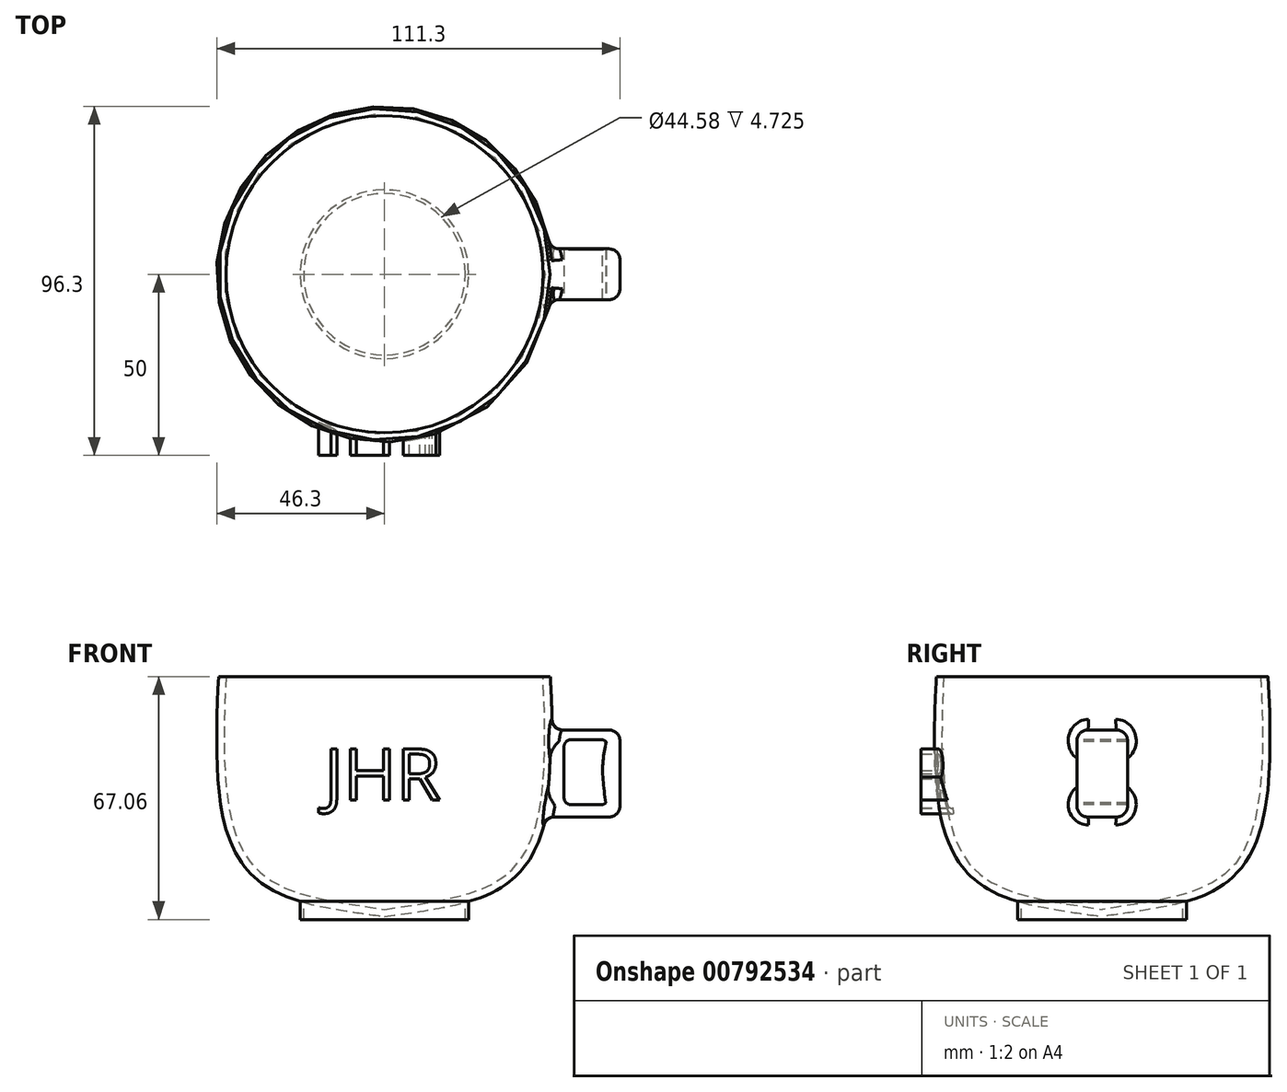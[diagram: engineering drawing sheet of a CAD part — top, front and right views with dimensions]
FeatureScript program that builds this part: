
annotation { "Feature Type Name" : "Feature", "Feature Type Description" : "" }
export const myFeature = defineFeature(function(context is Context, id is Id, definition is map)
    precondition{}
    {
        {
            var Q0;
            Q0=qCreatedBy(makeId("Front.planeOp"),FACE);
            var sketch = newSketch(context, id + "F0", { "sketchPlane" : qUnion([Q0])});
            skFitSpline(sketch, "E0", {"points": [v(-4.5, -38.34) * mm, v(36.26, -25.42) * mm, v(43.52, 31.56) * mm], "startDerivative": vector(104.57, 20.01) * mm, "endDerivative": vector(-6, 125.75) * mm});
            skFitSpline(sketch, "E1.0", {"points": [v(-4.13, -40.3) * mm, v(0.17, -39.48) * mm, v(6.7, -38.54) * mm, v(15.07, -37.17) * mm, v(21.07, -35.9) * mm, v(26.7, -34.18) * mm, v(30.98, -32.2) * mm, v(34.08, -30.19) * mm, v(35.86, -28.72) * mm, v(37.18, -27.4) * mm, v(38.42, -26) * mm, v(39.8, -24.1) * mm, v(41.23, -21.58) * mm, v(42.84, -17.96) * mm, v(44.34, -12.98) * mm, v(45.48, -6.4) * mm, v(46.1, 0.69) * mm, v(46.3, 8.15) * mm, v(46.16, 18.46) * mm, v(45.77, 26.42) * mm, v(45.52, 31.66) * mm]});
            skLineSegment(sketch, "E2", {"start": v(0, 55.43) * mm, "end": v(0, -65.78) * mm});
            skLineSegment(sketch, "E3", {"start": v(22.29, -35.48) * mm, "end": v(22.29, -40.3) * mm});
            skLineSegment(sketch, "E4", {"start": v(43.75, 26.76) * mm, "end": v(45.75, 26.76) * mm});
            skLineSegment(sketch, "E5.1", {"start": v(23.29, -35.19) * mm, "end": v(23.29, -40.3) * mm});
            skLineSegment(sketch, "E6", {"start": v(21.86, -40.3) * mm, "end": v(24.18, -40.3) * mm});
            skPoint(sketch, "E7.visualSharp", {"position": v(68.86, -16.24) * mm});
            skSolve(sketch);
        }
        {
            var Q0;
            Q0 = qSketchRegion(id + "F0", true);
            var Q1;
            Q1=sQuery(id+"F0.wireOp",EDGE,"E2");
            revolve(context, id + "F1", {"surfaceOperationType" : NewSurfaceOperationType.NEW, "entities" : qUnion([Q0]), "axis" : qUnion([Q1]), "revolveType" : RevolveType.FULL});
        }
        {
            var Q0;
            Q0=qCreatedBy(makeId("Right.planeOp"),FACE);
            var sketch = newSketch(context, id + "F2", { "sketchPlane" : qUnion([Q0])});
            skLineSegment(sketch, "E8.bottom", {"start": v(-7, 12) * mm, "end": v(7, 12) * mm});
            skLineSegment(sketch, "E8.top", {"start": v(-7, -12) * mm, "end": v(7, -12) * mm});
            skLineSegment(sketch, "E8.left", {"start": v(-7, 12) * mm, "end": v(-7, -12) * mm});
            skLineSegment(sketch, "E8.right", {"start": v(7, 12) * mm, "end": v(7, -12) * mm});
            skSolve(sketch);
        }
        {
            var Q0;
            Q0 = qSketchRegion(id + "F2", true);
            extrude(context, id + "F3", {"entities" : qUnion([Q0]), "operationType" : NewBodyOperationType.ADD, "depth" : 65 * mm, "offsetDistance" : 25 * mm});
        }
        {
            var Q0;
            {var subQ0=sQuery(id+"F0.wireOp",EDGE,"E1.0");var subQ2=sQuery(id+"F2.wireOp",EDGE,"E8.left");Q0=makeQuery(id+"F3.boolean.opBoolean","SPLIT",FACE,{"disambiguationData":[TD([makeQuery(id+"F1.opRevolve","SWEPT_FACE",FACE,{"disambiguationData":[OSD([subQ0]),TDD([makeQuery(id+"F0.imprint","IMPRINT",EDGE,{"disambiguationData":[TD([[makeQuery(id+"F0.imprint","INTERSECT",VERTEX,{"derivedFrom":[subQ0,sQuery(id+"F0.wireOp",EDGE,"E4")]}),1.0]])],"derivedFrom":subQ0})])]})])],"derivedFrom":makeQuery(id+"F3.opExtrude","SWEPT_FACE",FACE,{"disambiguationData":[OSD([subQ2])]})});}
            var sketch = newSketch(context, id + "F4", { "sketchPlane" : qUnion([Q0])});
            skLineSegment(sketch, "E9.bottom", {"start": v(51.55, 9.35) * mm, "end": v(59.73, 9.35) * mm});
            skLineSegment(sketch, "E9.top", {"start": v(51.55, -8.65) * mm, "end": v(59.73, -8.65) * mm});
            skLineSegment(sketch, "E9.left", {"start": v(49.55, 7.35) * mm, "end": v(49.55, -6.65) * mm});
            skLineSegment(sketch, "E9.right", {"start": v(61.73, 7.35) * mm, "end": v(61.73, -6.65) * mm});
            skPoint(sketch, "E10.visualSharp", {"position": v(49.55, 9.35) * mm});
            skArc(sketch, "E10.filletArc", {"start": v(51.55, 9.35) * mm, "mid": v(50.14, 8.76) * mm, "end": v(49.55, 7.35) * mm});
            skPoint(sketch, "E11.visualSharp", {"position": v(61.73, 9.35) * mm});
            skArc(sketch, "E11.filletArc", {"start": v(61.73, 7.35) * mm, "mid": v(61.14, 8.76) * mm, "end": v(59.73, 9.35) * mm});
            skPoint(sketch, "E12.visualSharp", {"position": v(61.73, -8.65) * mm});
            skArc(sketch, "E12.filletArc", {"start": v(59.73, -8.65) * mm, "mid": v(61.14, -8.07) * mm, "end": v(61.73, -6.65) * mm});
            skPoint(sketch, "E13.visualSharp", {"position": v(49.55, -8.65) * mm});
            skArc(sketch, "E13.filletArc", {"start": v(49.55, -6.65) * mm, "mid": v(50.14, -8.07) * mm, "end": v(51.55, -8.65) * mm});
            skSolve(sketch);
        }
        {
            var Q0;
            Q0 = qSketchRegion(id + "F4", true);
            extrude(context, id + "F5", {"entities" : qUnion([Q0]), "operationType" : NewBodyOperationType.REMOVE, "endBound" : BoundingType.UP_TO_NEXT, "oppositeDirection" : true, "depth" : 25 * mm, "offsetDistance" : 25 * mm});
        }
        {
            var Q0;
            Q0=qCreatedBy(makeId("Front.planeOp"),FACE);
            var sketch = newSketch(context, id + "F6", { "sketchPlane" : qUnion([Q0])});
            skText(sketch, "E14", { "text": "JHR", "fontName": "OpenSans-Regular.ttf"});
            const initialGuessF6  = {"E14": [-0.01664, -0.00738, 1, 0, 0.01427]};
            skSetInitialGuess(sketch, initialGuessF6);
            skSolve(sketch);
        }
        {
            var Q0;
            Q0 = qSketchRegion(id + "F6", true);
            extrude(context, id + "F7", {"entities" : qUnion([Q0]), "operationType" : NewBodyOperationType.ADD, "depth" : 50 * mm, "offsetDistance" : 25 * mm});
        }
        {
            var Q0;
            Q0 = qSketchRegion(id + "F6", true);
            var Q1;
            Q1=makeQuery(id+"F7.boolean.opBoolean","SPLIT",FACE,{"disambiguationData":[TD([makeQuery(id+"F1.opRevolve","SWEPT_FACE",FACE,{"disambiguationData":[OSD([sQuery(id+"F0.wireOp",EDGE,"E4")])]})])],"derivedFrom":makeQuery(id+"F1.opRevolve","SWEPT_FACE",FACE,{"disambiguationData":[OSD([sQuery(id+"F0.wireOp",EDGE,"E0")])]})});
            extrude(context, id + "F8", {"entities" : qUnion([Q0]), "operationType" : NewBodyOperationType.REMOVE, "endBound" : BoundingType.UP_TO_SURFACE, "depth" : 25 * mm, "endBoundEntityFace" : qUnion([Q1]), "offsetDistance" : 25 * mm});
        }
        {
            var Q0;
            Q0 = qSketchRegion(id + "F2", true);
            var Q1;
            {var subQ0=sQuery(id+"F6.wireOp",EDGE,"E14.sketch_text.stroke-39");var subQ1=sQuery(id+"F6.wireOp",EDGE,"E14.sketch_text.stroke-38");var subQ2=sQuery(id+"F6.wireOp",EDGE,"E14.sketch_text.stroke-37");var subQ3=sQuery(id+"F6.wireOp",EDGE,"E14.sketch_text.stroke-36");var subQ4=sQuery(id+"F6.wireOp",EDGE,"E14.sketch_text.stroke-35");var subQ5=sQuery(id+"F6.wireOp",EDGE,"E14.sketch_text.stroke-34");var subQ6=sQuery(id+"F6.wireOp",EDGE,"E14.sketch_text.stroke-33");var subQ7=sQuery(id+"F6.wireOp",EDGE,"E14.sketch_text.stroke-32");var subQ8=sQuery(id+"F6.wireOp",EDGE,"E14.sketch_text.stroke-31");var subQ9=sQuery(id+"F6.wireOp",EDGE,"E14.sketch_text.stroke-30");var subQ10=sQuery(id+"F6.wireOp",EDGE,"E14.sketch_text.stroke-29");var subQ11=sQuery(id+"F6.wireOp",EDGE,"E14.sketch_text.stroke-28");var subQ12=sQuery(id+"F6.wireOp",EDGE,"E14.sketch_text.stroke-27");var subQ13=sQuery(id+"F6.wireOp",EDGE,"E14.sketch_text.stroke-26");var subQ14=sQuery(id+"F6.wireOp",EDGE,"E14.sketch_text.stroke-25");var subQ15=sQuery(id+"F6.wireOp",EDGE,"E14.sketch_text.stroke-24");var subQ16=sQuery(id+"F6.wireOp",EDGE,"E14.sketch_text.stroke-23");var subQ17=sQuery(id+"F6.wireOp",EDGE,"E14.sketch_text.stroke-22");var subQ18=sQuery(id+"F6.wireOp",EDGE,"E14.sketch_text.stroke-21");var subQ19=sQuery(id+"F6.wireOp",EDGE,"E14.sketch_text.stroke-20");var subQ20=sQuery(id+"F6.wireOp",EDGE,"E14.sketch_text.stroke-19");var subQ21=sQuery(id+"F6.wireOp",EDGE,"E14.sketch_text.stroke-18");var subQ22=sQuery(id+"F6.wireOp",EDGE,"E14.sketch_text.stroke-17");var subQ23=sQuery(id+"F6.wireOp",EDGE,"E14.sketch_text.stroke-16");var subQ24=sQuery(id+"F6.wireOp",EDGE,"E14.sketch_text.stroke-15");var subQ25=sQuery(id+"F6.wireOp",EDGE,"E14.sketch_text.stroke-14");var subQ26=sQuery(id+"F6.wireOp",EDGE,"E14.sketch_text.stroke-13");var subQ27=sQuery(id+"F6.wireOp",EDGE,"E14.sketch_text.stroke-12");var subQ28=sQuery(id+"F6.wireOp",EDGE,"E14.sketch_text.stroke-11");var subQ29=sQuery(id+"F6.wireOp",EDGE,"E14.sketch_text.stroke-10");var subQ30=sQuery(id+"F6.wireOp",EDGE,"E14.sketch_text.stroke-9");var subQ31=sQuery(id+"F6.wireOp",EDGE,"E14.sketch_text.stroke-8");var subQ32=sQuery(id+"F6.wireOp",EDGE,"E14.sketch_text.stroke-7");var subQ33=sQuery(id+"F6.wireOp",EDGE,"E14.sketch_text.stroke-6");var subQ34=sQuery(id+"F6.wireOp",EDGE,"E14.sketch_text.stroke-5");var subQ35=sQuery(id+"F6.wireOp",EDGE,"E14.sketch_text.stroke-4");var subQ36=sQuery(id+"F6.wireOp",EDGE,"E14.sketch_text.stroke-3");var subQ37=sQuery(id+"F6.wireOp",EDGE,"E14.sketch_text.stroke-2");var subQ38=sQuery(id+"F6.wireOp",EDGE,"E14.sketch_text.stroke-1");var subQ39=sQuery(id+"F6.wireOp",EDGE,"E14.sketch_text.stroke-0");var subQ40=makeQuery(id+"F1.opRevolve","SWEPT_FACE",FACE,{"disambiguationData":[OSD([sQuery(id+"F0.wireOp",EDGE,"E0")])]});Q1=makeQuery(id+"F8.boolean.opBoolean","MERGE",FACE,{"derivedFrom":[makeQuery(id+"F7.boolean.opBoolean","SPLIT",FACE,{"disambiguationData":[TD([makeQuery(id+"F7.opExtrude","SWEPT_FACE",FACE,{"disambiguationData":[OSD([subQ6])]})])],"derivedFrom":subQ40}),makeQuery(id+"F7.boolean.opBoolean","SPLIT",FACE,{"disambiguationData":[TD([makeQuery(id+"F1.opRevolve","SWEPT_FACE",FACE,{"disambiguationData":[OSD([sQuery(id+"F0.wireOp",EDGE,"E4")])]})])],"derivedFrom":subQ40}),makeQuery(id+"F8.opExtrude","CAP_FACE",FACE,{"disambiguationData":[OSD([subQ39,subQ38,subQ37,subQ36,subQ35,subQ34,subQ33,subQ32,subQ31,subQ30])],"isStart":false}),makeQuery(id+"F8.opExtrude","CAP_FACE",FACE,{"disambiguationData":[OSD([subQ29,subQ28,subQ27,subQ26,subQ25,subQ24,subQ23,subQ22,subQ21,subQ20,subQ19,subQ18])],"isStart":false}),makeQuery(id+"F8.opExtrude","CAP_FACE",FACE,{"disambiguationData":[OSD([subQ17,subQ16,subQ15,subQ14,subQ13,subQ12,subQ11,subQ10,subQ9,subQ8,subQ7,subQ6,subQ5,subQ4,subQ3,subQ2,subQ1,subQ0])],"isStart":false})]});}
            extrude(context, id + "F9", {"entities" : qUnion([Q0]), "operationType" : NewBodyOperationType.REMOVE, "endBound" : BoundingType.UP_TO_SURFACE, "depth" : 25 * mm, "endBoundEntityFace" : qUnion([Q1]), "offsetDistance" : 25 * mm});
        }
        {
            var Q0;
            {var subQ0=sQuery(id+"F0.wireOp",EDGE,"E1.0");var subQ2=sQuery(id+"F2.wireOp",EDGE,"E8.left");Q0=makeQuery(id+"F3.boolean.opBoolean","SPLIT",FACE,{"disambiguationData":[TD([makeQuery(id+"F1.opRevolve","SWEPT_FACE",FACE,{"disambiguationData":[OSD([subQ0]),TDD([makeQuery(id+"F0.imprint","IMPRINT",EDGE,{"disambiguationData":[TD([[makeQuery(id+"F0.imprint","INTERSECT",VERTEX,{"derivedFrom":[subQ0,sQuery(id+"F0.wireOp",EDGE,"E4")]}),1.0]])],"derivedFrom":subQ0})])]})])],"derivedFrom":makeQuery(id+"F3.opExtrude","SWEPT_FACE",FACE,{"disambiguationData":[OSD([subQ2])]})});}
            var sketch = newSketch(context, id + "F10", { "sketchPlane" : qUnion([Q0])});
            skPoint(sketch, "E15.2.internal.snap0", {"position": v(61.73, 0.35) * mm});
            skFitSpline(sketch, "E16", {"points": [v(60.99, -1.7) * mm, v(61.11, -1.53) * mm], "startDerivative": vector(0.13, 0.18) * mm, "endDerivative": vector(0.13, 0.18) * mm});
            skFitSpline(sketch, "E17", {"points": [v(61.14, 8.76) * mm, v(60.22, 1.55) * mm, v(61.07, -8.14) * mm], "startDerivative": vector(-2.83, -14.97) * mm, "endDerivative": vector(2.55, -18.73) * mm});
            skSolve(sketch);
        }
        {
            var Q0;
            {var subQ0=sQuery(id+"F10.wireOp",EDGE,"E17");Q0=makeQuery(id+"F10.imprint","IMPRINT",FACE,{"disambiguationData":[TD([[makeQuery(id+"F10.imprint","IMPRINT",EDGE,{"derivedFrom":subQ0}),1.0]])]});}
            var Q1;
            Q1=sQuery(id+"F10.wireOp",EDGE,"E17");
            var Q2;
            Q2=makeQuery(id+"F1.opRevolve","SWEPT_BODY",BODY,{"disambiguationData":[OSD([sQuery(id+"F0.wireOp",EDGE,"E0"),sQuery(id+"F0.wireOp",EDGE,"E1.0"),sQuery(id+"F0.wireOp",EDGE,"E2"),sQuery(id+"F0.wireOp",EDGE,"E3"),sQuery(id+"F0.wireOp",EDGE,"E4"),sQuery(id+"F0.wireOp",EDGE,"E5.1"),sQuery(id+"F0.wireOp",EDGE,"E6")])]});
            extrude(context, id + "F11", {"entities" : qUnion([Q0]), "operationType" : NewBodyOperationType.ADD, "surfaceEntities" : qUnion([Q1]), "oppositeDirection" : true, "depth" : 14 * mm, "offsetDistance" : 25 * mm});
        }
        {
            var Q0;
            {var subQ0=sQuery(id+"F0.wireOp",EDGE,"E1.0");var subQ3=sQuery(id+"F2.wireOp",EDGE,"E8.bottom");Q0=makeQuery(id+"F3.boolean.opBoolean","SPLIT",FACE,{"disambiguationData":[TD([makeQuery(id+"F1.opRevolve","SWEPT_FACE",FACE,{"disambiguationData":[OSD([subQ0]),TDD([makeQuery(id+"F0.imprint","IMPRINT",EDGE,{"disambiguationData":[TD([[makeQuery(id+"F0.imprint","INTERSECT",VERTEX,{"derivedFrom":[subQ0,sQuery(id+"F0.wireOp",EDGE,"E4")]}),1.0]])],"derivedFrom":subQ0})])]})])],"derivedFrom":makeQuery(id+"F3.opExtrude","SWEPT_FACE",FACE,{"disambiguationData":[OSD([subQ3])]})});}
            var Q1;
            Q1=makeQuery(id+"F3.opExtrude","CAP_FACE",FACE,{"disambiguationData":[OSD([sQuery(id+"F2.wireOp",EDGE,"E8.bottom"),sQuery(id+"F2.wireOp",EDGE,"E8.top"),sQuery(id+"F2.wireOp",EDGE,"E8.left"),sQuery(id+"F2.wireOp",EDGE,"E8.right")])],"isStart":false});
            var Q2;
            {var subQ0=sQuery(id+"F0.wireOp",EDGE,"E1.0");var subQ3=sQuery(id+"F2.wireOp",EDGE,"E8.top");Q2=makeQuery(id+"F3.boolean.opBoolean","SPLIT",FACE,{"disambiguationData":[TD([makeQuery(id+"F1.opRevolve","SWEPT_FACE",FACE,{"disambiguationData":[OSD([subQ0]),TDD([makeQuery(id+"F0.imprint","IMPRINT",EDGE,{"disambiguationData":[TD([[makeQuery(id+"F0.imprint","INTERSECT",VERTEX,{"derivedFrom":[subQ0,sQuery(id+"F0.wireOp",EDGE,"E4")]}),1.0]])],"derivedFrom":subQ0})])]})])],"derivedFrom":makeQuery(id+"F3.opExtrude","SWEPT_FACE",FACE,{"disambiguationData":[OSD([subQ3])]})});}
            fillet(context, id + "F12", {"entities" : qUnion([Q0, Q1, Q2]), "radius" : 3 * mm, "tangentPropagation" : true, "allowEdgeOverflow" : false});
        }
    });
